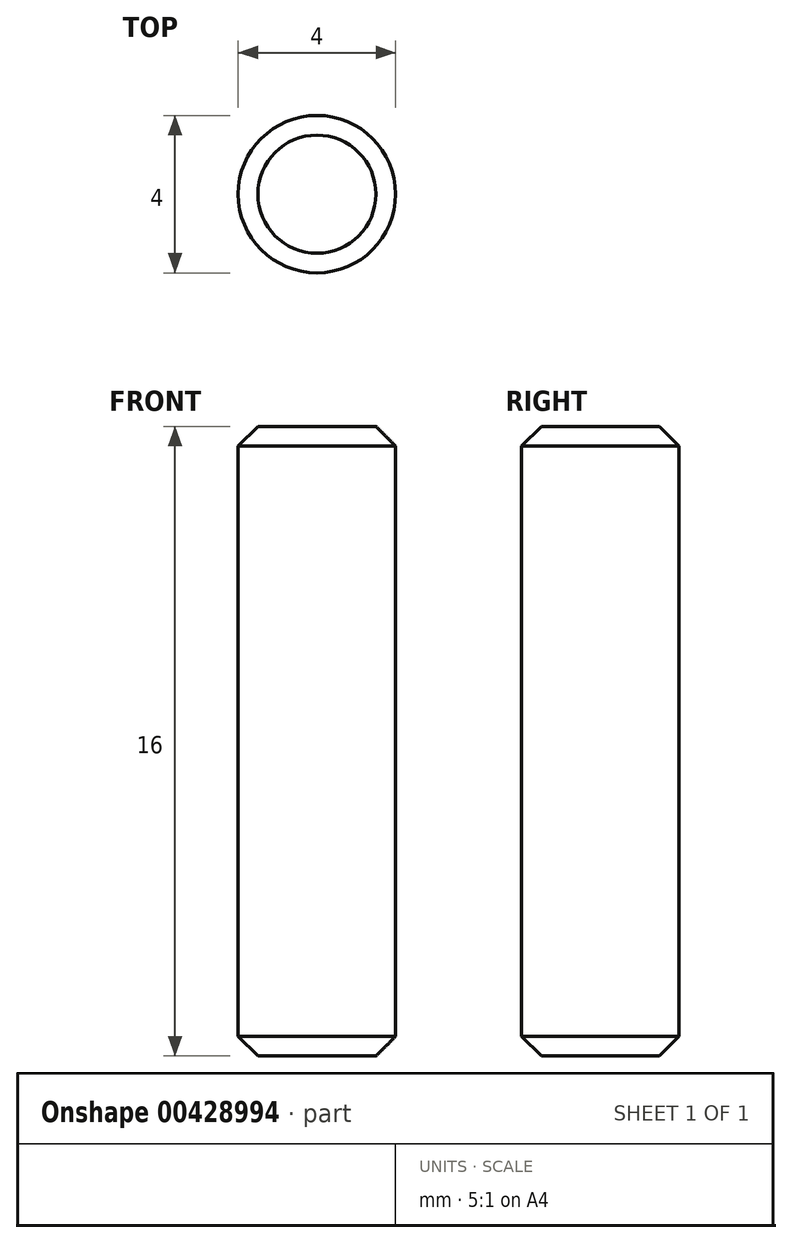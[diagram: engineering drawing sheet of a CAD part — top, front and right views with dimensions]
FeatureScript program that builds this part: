
annotation { "Feature Type Name" : "Feature", "Feature Type Description" : "" }
export const myFeature = defineFeature(function(context is Context, id is Id, definition is map)
    precondition{}
    {
        {
            var Q0;
            Q0=qCreatedBy(makeId("Top.planeOp"),FACE);
            var sketch = newSketch(context, id + "F0", { "sketchPlane" : qUnion([Q0])});
            skCircle(sketch, "E0", {"center": v(0, 0) * mm, "radius": 2 * mm});
            skSolve(sketch);
        }
        {
            var Q0;
            Q0 = qSketchRegion(id + "F0", true);
            extrude(context, id + "F1", {"entities" : qUnion([Q0]), "endBound" : BoundingType.SYMMETRIC, "depth" : 16 * mm});
        }
        {
            var Q0;
            Q0=makeQuery(id+"F1.opExtrude","CAP_EDGE",EDGE,{"disambiguationData":[OSD([sQuery(id+"F0.wireOp",EDGE,"E0")])],"isStart":false});
            var Q1;
            Q1=makeQuery(id+"F1.opExtrude","CAP_EDGE",EDGE,{"disambiguationData":[OSD([sQuery(id+"F0.wireOp",EDGE,"E0")])],"isStart":true});
            chamfer(context, id + "F2", {"entities" : qUnion([Q0, Q1]), "width" : 0.5 * mm, "tangentPropagation" : true});
        }
    });
